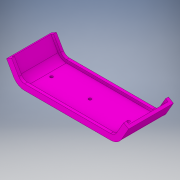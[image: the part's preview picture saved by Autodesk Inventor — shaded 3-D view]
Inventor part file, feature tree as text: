
AUTODESK INVENTOR PART (.ipt)
format: ipt  version: 2019 (Build 230136000, 136)  size: 199,680 bytes
history: native  units: mm
features: sketch x5, extrude x3, hole x2, projected_geometry x2, plane x1, mirror x1
ambient origin geometry x8: Origin, YZ Plane, XZ Plane, XY Plane, X Axis, Y Axis, Z Axis, Center Point
bodies: Solid1 (feature_tree)
feature tree (14):
  extrude  "Extrusion1"  Depth=40.0mm
  hole  "Hole1"  [1 undecoded]
  hole  "Hole2"  [1 undecoded]
  plane  "Work Plane2"
  extrude  "Extrusion3"  Depth=3.0mm TaperAngle=0.0deg
  extrude  "Extrusion4"  Depth=3.0mm
  mirror  "Mirror2"
  sketch  "Sketch1"  dims[d1=40.0mm d2=0.0mm d3=40.0mm]
  sketch  "Sketch2"  dims[d4=40.0mm]
  sketch  "Sketch3"  dims[d5=3.0mm d6=6.0mm d7=11.5mm d8=2.0mm d9=90.0deg d10=8.0mm d11=20.594885mm d12=20.0mm]
  sketch  "Sketch5"  dims[d13=20.0mm d14=7.0mm]
  projected_geometry  "Projected Loop2"
  sketch  "Sketch6"  dims[d15=3.0mm d16=6.0mm d17=4.0mm d18=2.0mm d19=90.0deg d20=8.0mm d21=20.594885mm d25=0.25mm d26=0.0mm d27=3.0mm d28=3.0mm d29=0.0mm d30=4.744646mm d31=4.744646mm]
  projected_geometry  "Projected Loop4"
note: 2 required parameter values undecoded (feature->parameter linkage not recoverable at this tier; creation-order binding heuristic only, values carry confidence <= 0.55)
